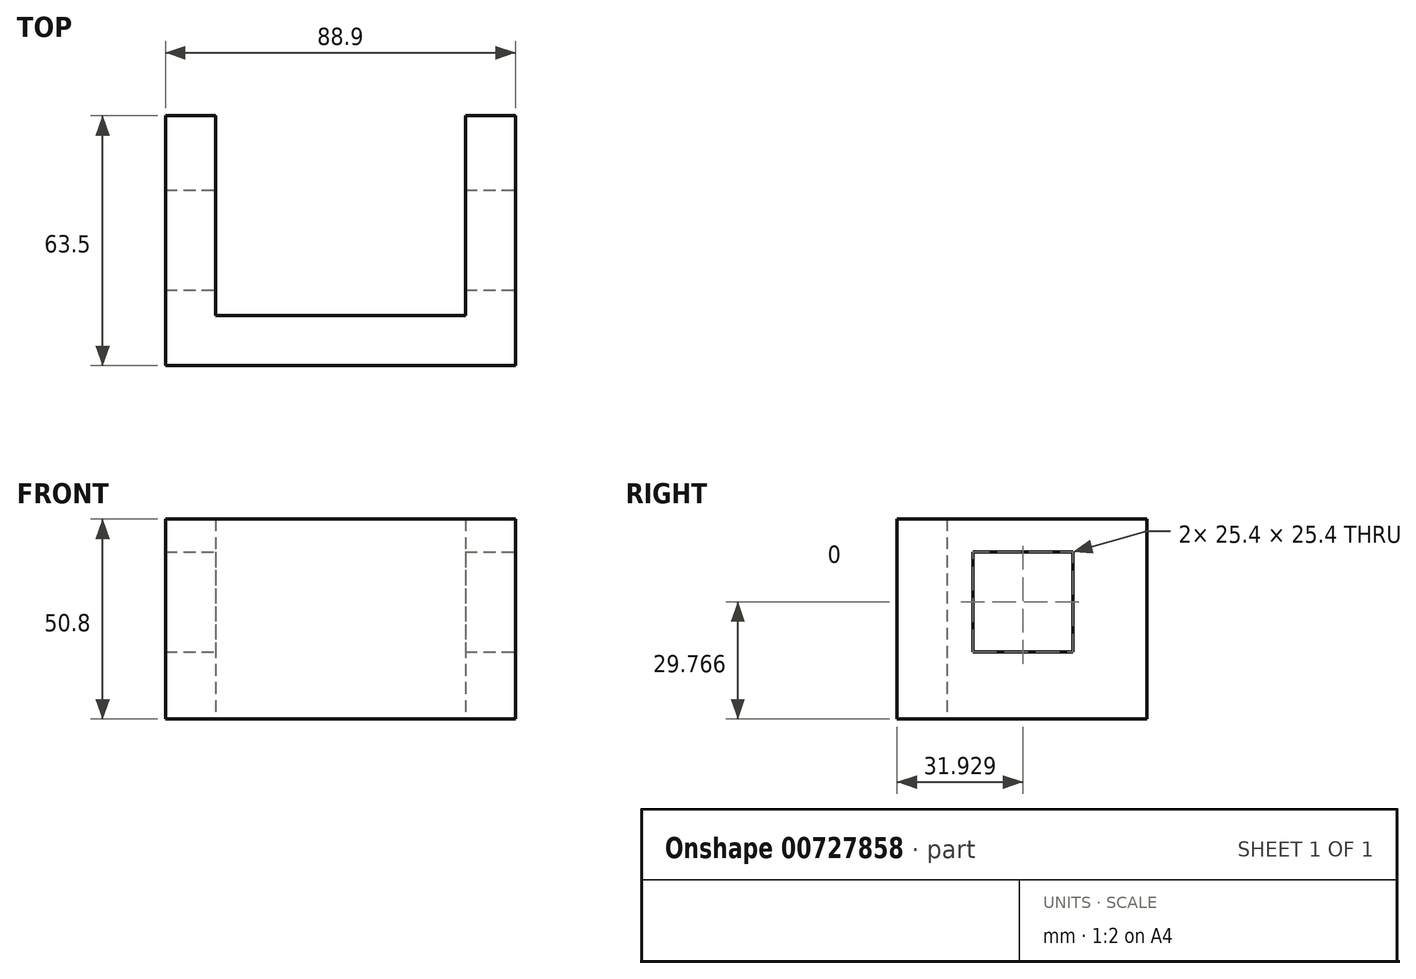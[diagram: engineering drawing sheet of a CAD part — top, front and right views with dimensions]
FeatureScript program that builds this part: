
annotation { "Feature Type Name" : "Feature", "Feature Type Description" : "" }
export const myFeature = defineFeature(function(context is Context, id is Id, definition is map)
    precondition{}
    {
        {
            var Q0;
            Q0=qCreatedBy(makeId("Top.planeOp"),FACE);
            var sketch = newSketch(context, id + "F0", { "sketchPlane" : qUnion([Q0])});
            skLineSegment(sketch, "E0", {"start": v(-55, -12.7) * mm, "end": v(33.9, -12.7) * mm});
            skLineSegment(sketch, "E1", {"start": v(-55, -12.7) * mm, "end": v(-55, 50.8) * mm});
            skLineSegment(sketch, "E2", {"start": v(-55, 50.8) * mm, "end": v(-42.3, 50.8) * mm});
            skLineSegment(sketch, "E3", {"start": v(-42.3, 50.8) * mm, "end": v(-42.3, 0) * mm});
            skLineSegment(sketch, "E4", {"start": v(33.9, -12.7) * mm, "end": v(33.9, 50.8) * mm});
            skLineSegment(sketch, "E5", {"start": v(33.9, 50.8) * mm, "end": v(21.2, 50.8) * mm});
            skLineSegment(sketch, "E6", {"start": v(21.2, 50.8) * mm, "end": v(21.2, 0) * mm});
            skLineSegment(sketch, "E7", {"start": v(-42.3, 0) * mm, "end": v(21.2, 0) * mm});
            skSolve(sketch);
        }
        {
            var Q0;
            Q0=makeQuery(id+"F0.imprint","IMPRINT",FACE,{"disambiguationData":[TD([[makeQuery(id+"F0.imprint","IMPRINT",EDGE,{"derivedFrom":sQuery(id+"F0.wireOp",EDGE,"E0")}),1.0]])]});
            extrude(context, id + "F1", {"entities" : qUnion([Q0]), "depth" : 50.8 * mm, "offsetDistance" : 25.4 * mm});
        }
        {
            var Q0;
            Q0=makeQuery(id+"F1.opExtrude","SWEPT_FACE",FACE,{"disambiguationData":[OSD([sQuery(id+"F0.wireOp",EDGE,"E4")])]});
            var sketch = newSketch(context, id + "F2", { "sketchPlane" : qUnion([Q0])});
            skLineSegment(sketch, "E8.bottom", {"start": v(31.93, 42.47) * mm, "end": v(6.53, 42.47) * mm});
            skLineSegment(sketch, "E8.top", {"start": v(31.93, 17.07) * mm, "end": v(6.53, 17.07) * mm});
            skLineSegment(sketch, "E8.left", {"start": v(31.93, 42.47) * mm, "end": v(31.93, 17.07) * mm});
            skLineSegment(sketch, "E8.right", {"start": v(6.53, 42.47) * mm, "end": v(6.53, 17.07) * mm});
            skPoint(sketch, "E8.middle", {"position": v(19.23, 29.77) * mm});
            skSolve(sketch);
        }
        {
            var Q0;
            Q0=makeQuery(id+"F2.imprint","IMPRINT",FACE,{"disambiguationData":[TD([[makeQuery(id+"F2.imprint","IMPRINT",EDGE,{"derivedFrom":sQuery(id+"F2.wireOp",EDGE,"E8.bottom")}),1.0]])]});
            extrude(context, id + "F3", {"entities" : qUnion([Q0]), "operationType" : NewBodyOperationType.REMOVE, "oppositeDirection" : true, "depth" : 104.65 * mm, "offsetDistance" : 25.4 * mm});
        }
    });
